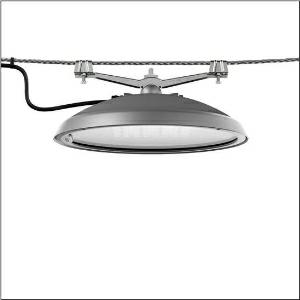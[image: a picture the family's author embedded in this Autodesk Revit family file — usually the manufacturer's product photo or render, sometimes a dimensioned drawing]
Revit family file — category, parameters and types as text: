
# Revit family: dl_50_iq_mini___st0_8s_5xa248v31f08fe_0db4
name_source: partatom
category: Lighting Fixtures
units: mm (PartAtom-declared; Revit-internal decimal feet)

## family parameters
Cut with Voids When Loaded = No
Host = Face
Light Source = No
Part Type = Normal
Room Calculation Point = No
Round Connector Dimension = Use Diameter
Shared = No

## types (1)
- --- (1 x LED, 2700 lm, 16.3 W, 3000K)
    Apparent Load = 16 VA
    CIE Flux Codes = 38 75 97 100 100
    Color Rendering = 70
    Color Temperature = 3000K
    Default Elevation = 1800 mm
    Description = DL 50 iQ mini, catenary luminaire, primary light control with lens, of PMMA, primary optical cover: cover, of toughened safety glass, transparent, light distribution: ST0.8s, light emission: direct distribution, primary light characteristic: symmetric, installation type: suspended mounting, LED, High Power LED, rated luminous flux: 2.700lm, luminous efficacy: 166lm/W, light colour: 730, colour temperature: 3000K, control gear: iQ Street-Remote, control: optimised constant luminous flux control (CLO 2.0), Desk-Remote (wireless, voltage-free reading and setting of iQ features in the workshop via application-optimized NFC function/RFID function), Light-Fading, Smart-Wire, Night-Set, Lumen-Switch, Temp-Guard, Auto-Match, Street-Remote, mains connection: 230..240V, AC, 50/60Hz, start of lifetime: 16W, end of service life: 17W, reduction: 8W, luminaire housing, of diecast aluminium, powder-coated, SITECO metallic grey (DB 702S), diameter: 500mm, height: 115mm, mounting height: 4..12m, protection rating (complete): IP66, insulation class (complete): insulation class II (safety insulation), certification: CE, ENEC, ENEC+, VDE, impact resistance: IK08, permissible operating ambient temperature for outdoor applications: -25..+40°C, standard-compliant lighting for roads and squares, packaging unit: 1 piece

Light Distribution: ST0.8s
    Height = 124 mm  [stored 0.406824 ft]
    Lamp = 1 x LED
    Lamp Light Flux = 2700 lm
    Lamp Power = 16.3 W
    Lamp count = 1
    Length = 500 mm
    Luminous efficacy = 166 lm/W
    Manufacturer = Siteco
    ModVariant = No
    Model = 5XA248V31F08FE
    Number of Poles = 1
    OnlyDefault = Yes
    Power Factor = 1
    Product Name = DL 50 iQ mini | ST0.8s
    Product group = catenary luminaire
    ProductGroupID = 6300
    Protection Class = Protection class II
    Protection Degree = IP 66
    RLX_Detail_Level = 1
    RLX_Emergency_Light_Flux = 0 lm
    RLX_Emergency_Type = 0
    RLX_Emergency_Type_DB = No
    RlxData = <blob elided: 123217 chars, md5=361120a7>
    Socket = socket
    Standby Power = 0 W
    System Light Flux = 2700 lm
    System Power = 16 W
    Type Comments = factory setting: luminous flux: 100 % | dim-lin: 254 | 333 mA
    Type Image = l_1242791.jpg
    URL = http://relux.com
    VarID = @adj_137461
    Voltage = 0 V
    Weight = 0.00 kg
    Width = 0 mm  [stored 0 ft]

note: [stored X ft] marks values corroborated as IEEE doubles in the binary element streams (Revit-internal decimal feet)

## geometry (parser evidence)
native form markers: Blend x4, Sweep x15
no freeform markers — native parametric forms only
